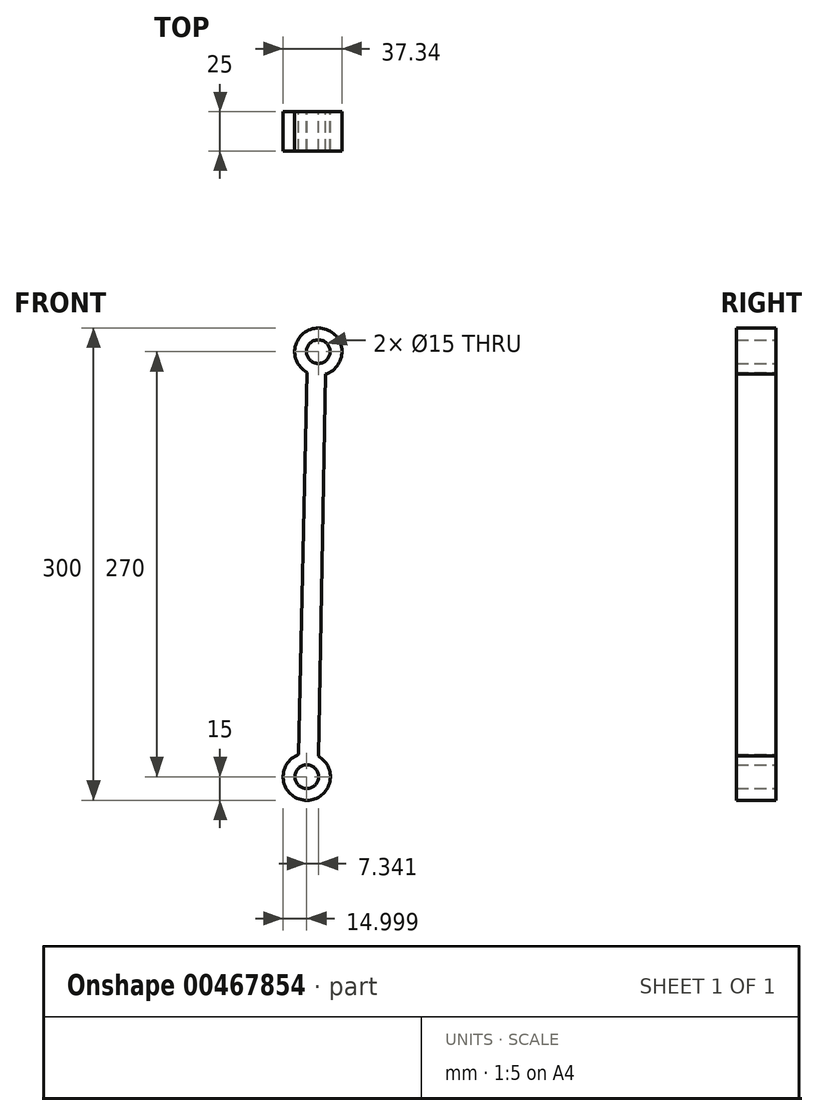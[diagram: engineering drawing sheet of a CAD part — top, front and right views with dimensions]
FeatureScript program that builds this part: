
annotation { "Feature Type Name" : "Feature", "Feature Type Description" : "" }
export const myFeature = defineFeature(function(context is Context, id is Id, definition is map)
    precondition{}
    {
        {
            var Q0;
            Q0=qCreatedBy(makeId("Front.planeOp"),FACE);
            var sketch = newSketch(context, id + "F0", { "sketchPlane" : qUnion([Q0])});
            skCircle(sketch, "E0", {"center": v(0, 0) * mm, "radius": 15 * mm});
            skCircle(sketch, "E1", {"center": v(0, 0) * mm, "radius": 7.5 * mm});
            skCircle(sketch, "E2", {"center": v(-7.34, -270) * mm, "radius": 15 * mm});
            skCircle(sketch, "E3", {"center": v(-7.34, -270) * mm, "radius": 7.5 * mm});
            skLineSegment(sketch, "E4", {"start": v(-7.26, -13.12) * mm, "end": v(-12.44, -255.9) * mm});
            skLineSegment(sketch, "E5", {"start": v(4.61, -14.27) * mm, "end": v(0, -256.92) * mm});
            skSolve(sketch);
        }
        {
            var Q0;
            Q0 = qSketchRegion(id + "F0", true);
            extrude(context, id + "F1", {"entities" : qUnion([Q0]), "depth" : 25 * mm});
        }
    });
